# Revit family: Accessory-Shelf-KOHLER-Purist-K-14440
name_source: partatom
category: Specialty Equipment
revit_build: Autodesk Revit 2015 (Build: 20140606_1530(x64)
units: mm (PartAtom-declared; Revit-internal decimal feet)

## types (5) — shared parameters
ADA Compliant = No
Assembly Code = C1030200
Date Modified = 05/27/2019
Default Elevation = 42"
Description = Glass shelf
Height = 4 7/8"
Length = 22 1/2"
Manufacturer = KOHLER Co.
MasterFormat 1995 = 10820
MasterFormat 2004 = 10.28.13
Material = Solid-brass construction
Product Documentation Link = https://www.us.kohler.com
Product Name = Purist
Product Page URL = http://www.us.kohler.com
URL = https://www.us.kohler.com
WaterSense Certified = No
Width = 1 7/8"

## per-type parameters (varying)
| type | Finish | Model | Type |
| CP - Polished Chrome | Kohler-Metal-CP-Polished_Chrome | K-14440-CP | 1 |
| SN - Vibrant Polished Nickel | Kohler-Metal-SN-Vibrant_Polished_Nickel | K-14440-SN | 2 |
| BGD - Vibrant Moderne Brushed Gold | Kohler-Metal-BGD-Vibrant_Moderne_Brushed_Gold | K-14440-BGD | 4 |
| BN - Vibrant Brushed Nickel | Kohler-Metal-BN-Vibrant_Brushed_Nickel | K-14440-BN | 3 |
| BV - Vibrant Brushed Bronze | Kohler-Metal-BV-Brushed_Bronze | K-14440-BV | 5 |

## geometry (parser evidence)
native form markers: Sweep x6
no freeform markers — native parametric forms only
